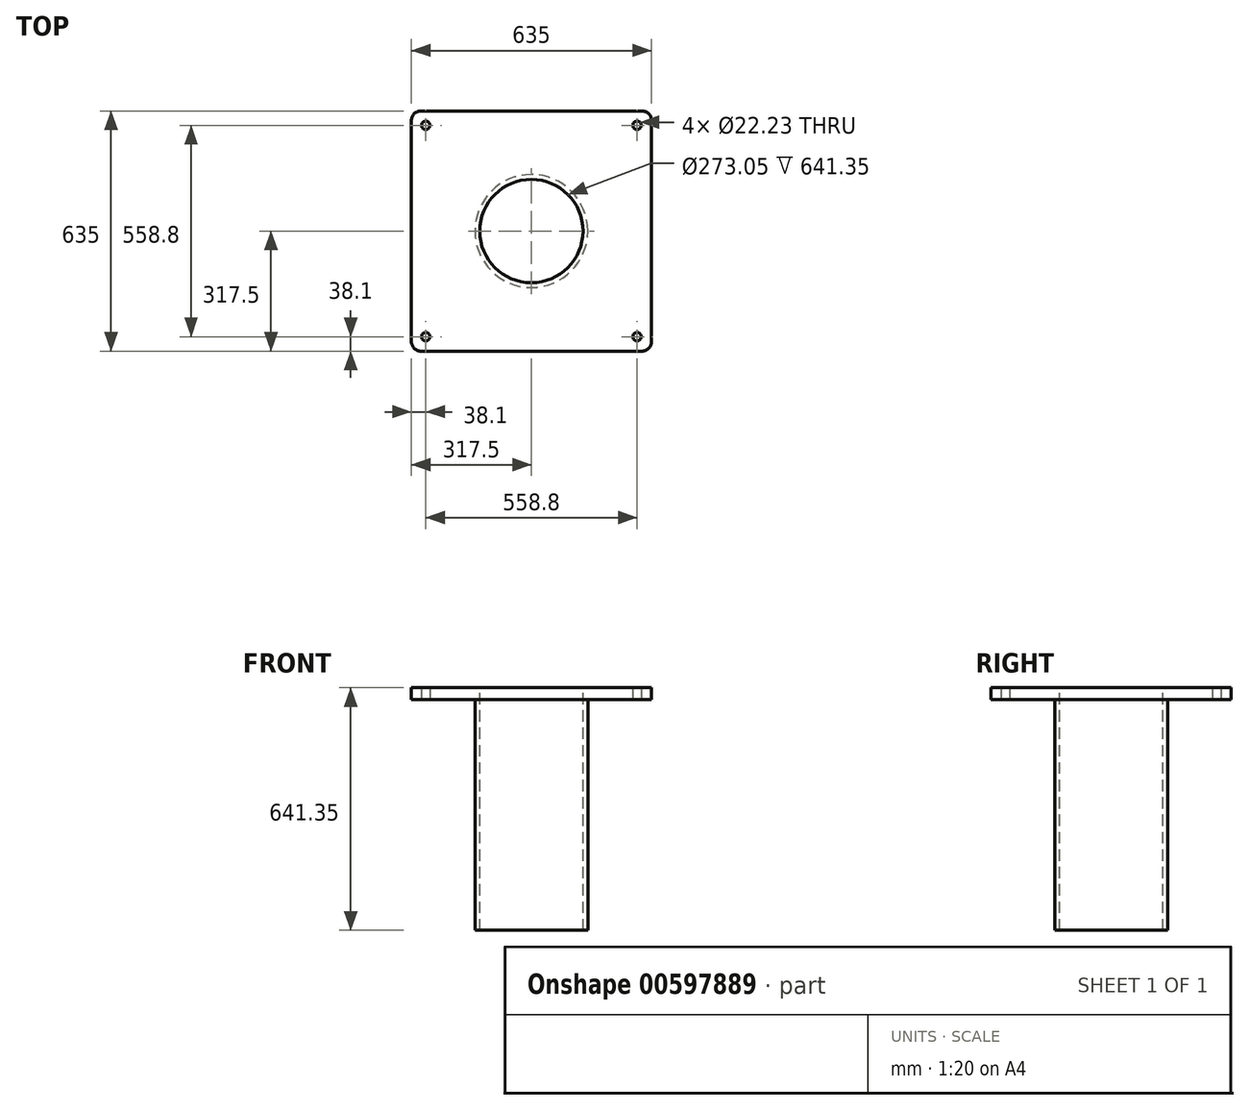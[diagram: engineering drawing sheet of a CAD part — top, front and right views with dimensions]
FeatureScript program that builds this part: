
annotation { "Feature Type Name" : "Feature", "Feature Type Description" : "" }
export const myFeature = defineFeature(function(context is Context, id is Id, definition is map)
    precondition{}
    {
        {
            var Q0;
            Q0=qCreatedBy(makeId("Top.planeOp"),FACE);
            var sketch = newSketch(context, id + "F0", { "sketchPlane" : qUnion([Q0])});
            skLineSegment(sketch, "E0.bottom", {"start": v(292.1, 317.5) * mm, "end": v(-292.1, 317.5) * mm});
            skLineSegment(sketch, "E0.top", {"start": v(292.1, -317.5) * mm, "end": v(-292.1, -317.5) * mm});
            skLineSegment(sketch, "E0.left", {"start": v(317.5, 292.1) * mm, "end": v(317.5, -292.1) * mm});
            skLineSegment(sketch, "E0.right", {"start": v(-317.5, 292.1) * mm, "end": v(-317.5, -292.1) * mm});
            skPoint(sketch, "E0.middle", {"position": v(0, 0) * mm});
            skLineSegment(sketch, "E1.bottom", {"start": v(279.4, 279.4) * mm, "end": v(-279.4, 279.4) * mm, "construction": true});
            skLineSegment(sketch, "E1.top", {"start": v(279.4, -279.4) * mm, "end": v(-279.4, -279.4) * mm, "construction": true});
            skLineSegment(sketch, "E1.left", {"start": v(279.4, 279.4) * mm, "end": v(279.4, -279.4) * mm, "construction": true});
            skLineSegment(sketch, "E1.right", {"start": v(-279.4, 279.4) * mm, "end": v(-279.4, -279.4) * mm, "construction": true});
            skCircle(sketch, "E2", {"center": v(-279.4, 279.4) * mm, "radius": 11.11 * mm});
            skCircle(sketch, "E3", {"center": v(279.4, 279.4) * mm, "radius": 11.11 * mm});
            skCircle(sketch, "E4", {"center": v(279.4, -279.4) * mm, "radius": 11.11 * mm});
            skCircle(sketch, "E5", {"center": v(-279.4, -279.4) * mm, "radius": 11.11 * mm});
            skPoint(sketch, "E6.visualSharp", {"position": v(-317.5, 317.5) * mm});
            skArc(sketch, "E6.filletArc", {"start": v(-292.1, 317.5) * mm, "mid": v(-310.06, 310.06) * mm, "end": v(-317.5, 292.1) * mm});
            skPoint(sketch, "E7.visualSharp", {"position": v(317.5, 317.5) * mm});
            skArc(sketch, "E7.filletArc", {"start": v(317.5, 292.1) * mm, "mid": v(310.06, 310.06) * mm, "end": v(292.1, 317.5) * mm});
            skPoint(sketch, "E8.visualSharp", {"position": v(317.5, -317.5) * mm});
            skArc(sketch, "E8.filletArc", {"start": v(292.1, -317.5) * mm, "mid": v(310.06, -310.06) * mm, "end": v(317.5, -292.1) * mm});
            skPoint(sketch, "E9.visualSharp", {"position": v(-317.5, -317.5) * mm});
            skArc(sketch, "E9.filletArc", {"start": v(-317.5, -292.1) * mm, "mid": v(-310.06, -310.06) * mm, "end": v(-292.1, -317.5) * mm});
            skSolve(sketch);
        }
        {
            var Q0;
            Q0 = qSketchRegion(id + "F0", true);
            extrude(context, id + "F1", {"entities" : qUnion([Q0]), "depth" : 31.75 * mm, "offsetDistance" : 25.4 * mm});
        }
        {
            var Q0;
            Q0=makeQuery(id+"F1.opExtrude","CAP_FACE",FACE,{"disambiguationData":[OSD([sQuery(id+"F0.wireOp",EDGE,"E0.bottom"),sQuery(id+"F0.wireOp",EDGE,"E0.top"),sQuery(id+"F0.wireOp",EDGE,"E0.left"),sQuery(id+"F0.wireOp",EDGE,"E0.right"),sQuery(id+"F0.wireOp",EDGE,"E2"),sQuery(id+"F0.wireOp",EDGE,"E3"),sQuery(id+"F0.wireOp",EDGE,"E4"),sQuery(id+"F0.wireOp",EDGE,"E5"),sQuery(id+"F0.wireOp",EDGE,"E6.filletArc"),sQuery(id+"F0.wireOp",EDGE,"E7.filletArc"),sQuery(id+"F0.wireOp",EDGE,"E8.filletArc"),sQuery(id+"F0.wireOp",EDGE,"E9.filletArc")])],"isStart":true});
            var sketch = newSketch(context, id + "F2", { "sketchPlane" : qUnion([Q0])});
            skCircle(sketch, "E10", {"center": v(0, 0) * mm, "radius": 149.23 * mm});
            skCircle(sketch, "E11", {"center": v(0, 0) * mm, "radius": 136.53 * mm});
            skSolve(sketch);
        }
        {
            var Q0;
            Q0 = qSketchRegion(id + "F2", true);
            extrude(context, id + "F3", {"entities" : qUnion([Q0]), "operationType" : NewBodyOperationType.ADD, "depth" : 609.6 * mm, "offsetDistance" : 25.4 * mm});
        }
        {
            var Q0;
            Q0=makeQuery(id+"F1.opExtrude","CAP_FACE",FACE,{"disambiguationData":[OSD([sQuery(id+"F0.wireOp",EDGE,"E0.bottom"),sQuery(id+"F0.wireOp",EDGE,"E0.top"),sQuery(id+"F0.wireOp",EDGE,"E0.left"),sQuery(id+"F0.wireOp",EDGE,"E0.right"),sQuery(id+"F0.wireOp",EDGE,"E2"),sQuery(id+"F0.wireOp",EDGE,"E3"),sQuery(id+"F0.wireOp",EDGE,"E4"),sQuery(id+"F0.wireOp",EDGE,"E5"),sQuery(id+"F0.wireOp",EDGE,"E6.filletArc"),sQuery(id+"F0.wireOp",EDGE,"E7.filletArc"),sQuery(id+"F0.wireOp",EDGE,"E8.filletArc"),sQuery(id+"F0.wireOp",EDGE,"E9.filletArc")])],"isStart":false});
            var sketch = newSketch(context, id + "F4", { "sketchPlane" : qUnion([Q0])});
            skCircle(sketch, "E12", {"center": v(0, 0) * mm, "radius": 136.53 * mm});
            skSolve(sketch);
        }
        {
            var Q0;
            Q0 = qSketchRegion(id + "F4", true);
            extrude(context, id + "F5", {"entities" : qUnion([Q0]), "operationType" : NewBodyOperationType.REMOVE, "oppositeDirection" : true, "depth" : 50.8 * mm, "offsetDistance" : 25.4 * mm});
        }
    });
